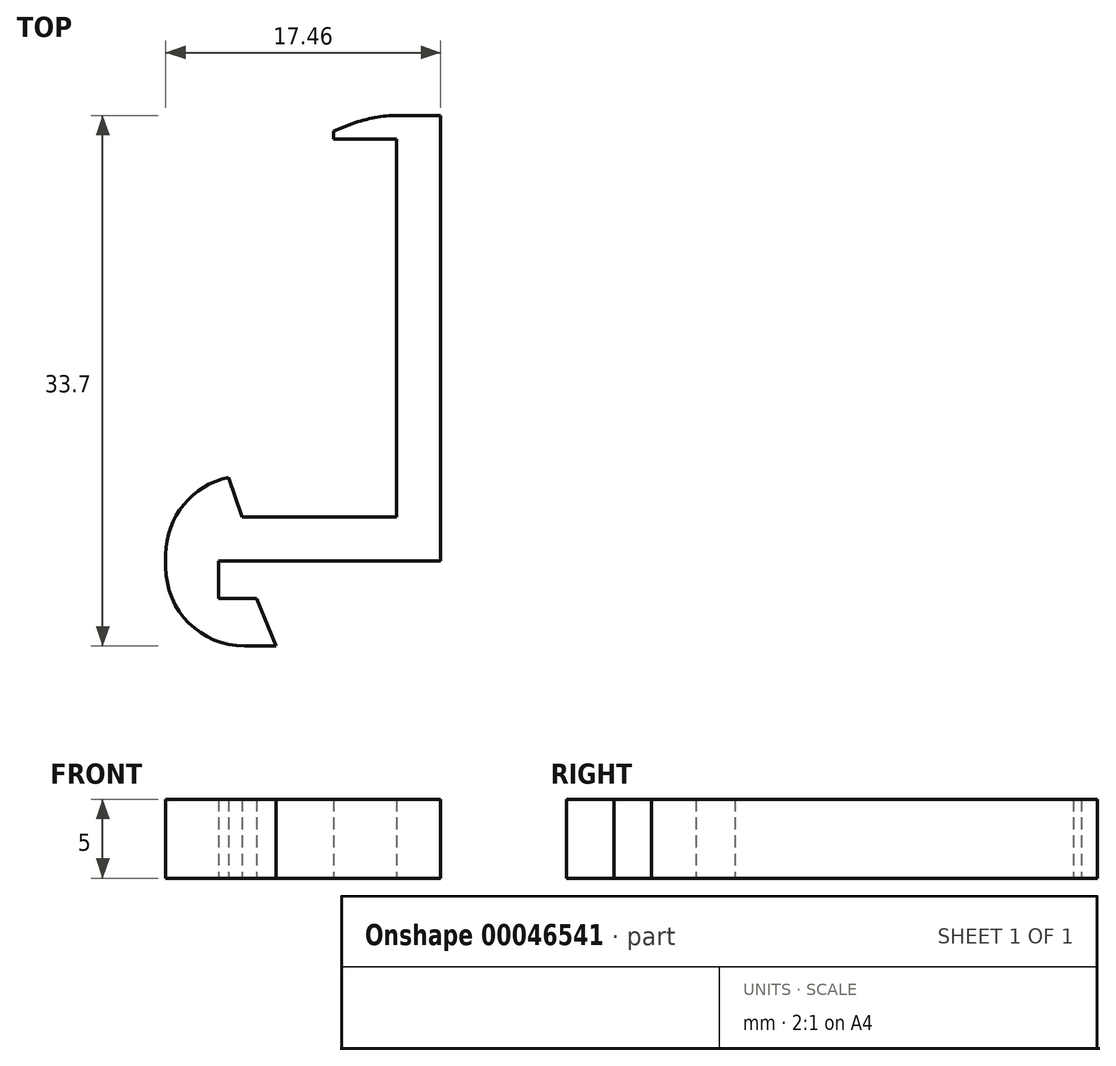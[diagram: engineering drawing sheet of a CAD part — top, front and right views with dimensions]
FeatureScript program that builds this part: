
annotation { "Feature Type Name" : "Feature", "Feature Type Description" : "" }
export const myFeature = defineFeature(function(context is Context, id is Id, definition is map)
    precondition{}
    {
        {
            var Q0;
            Q0=qCreatedBy(makeId("Top.planeOp"),FACE);
            var sketch = newSketch(context, id + "F0", { "sketchPlane" : qUnion([Q0])});
            skLineSegment(sketch, "E0", {"start": v(-10.46, -5.4) * mm, "end": v(-17.46, -5.4) * mm});
            skLineSegment(sketch, "E1", {"start": v(-17.46, -5.4) * mm, "end": v(-17.46, 5.3) * mm});
            skLineSegment(sketch, "E2", {"start": v(-17.46, 5.3) * mm, "end": v(-13.46, 5.3) * mm});
            skLineSegment(sketch, "E3", {"start": v(-13.46, 5.3) * mm, "end": v(-12.6, 2.8) * mm});
            skLineSegment(sketch, "E4", {"start": v(-12.6, 2.8) * mm, "end": v(-2.8, 2.8) * mm});
            skLineSegment(sketch, "E5", {"start": v(-2.8, 2.8) * mm, "end": v(-2.8, 26.8) * mm});
            skLineSegment(sketch, "E6", {"start": v(-2.8, 26.8) * mm, "end": v(-6.8, 26.8) * mm});
            skLineSegment(sketch, "E7", {"start": v(-14.1, 0) * mm, "end": v(-14.1, -2.4) * mm});
            skLineSegment(sketch, "E8", {"start": v(-14.1, -2.4) * mm, "end": v(-11.7, -2.4) * mm});
            skLineSegment(sketch, "E9", {"start": v(-11.7, -2.4) * mm, "end": v(-10.46, -5.4) * mm});
            skLineSegment(sketch, "E10", {"start": v(0, 28.3) * mm, "end": v(0, 0) * mm});
            skLineSegment(sketch, "E11", {"start": v(-14.1, 0) * mm, "end": v(0, 0) * mm});
            skLineSegment(sketch, "E12", {"start": v(0, 28.3) * mm, "end": v(-2.72, 28.3) * mm});
            skLineSegment(sketch, "E13", {"start": v(-6.8, 26.8) * mm, "end": v(-6.8, 27.3) * mm});
            skLineSegment(sketch, "E14", {"start": v(-6.8, 27.3) * mm, "end": v(-5.6, 27.76) * mm});
            skPoint(sketch, "E15.visualSharp", {"position": v(-4.2, 28.3) * mm});
            skArc(sketch, "E15.filletArc", {"start": v(-2.72, 28.3) * mm, "mid": v(-4.18, 28.16) * mm, "end": v(-5.6, 27.76) * mm});
            skSolve(sketch);
        }
        {
            var Q0;
            Q0=qSketchRegion(id+"F0",true);
            extrude(context, id + "F1", {"entities" : qUnion([Q0]), "depth" : 5 * mm});
        }
        {
            var Q0;
            Q0=makeQuery(id+"F1.opExtrude","SWEPT_EDGE",EDGE,{"disambiguationData":[OSD([sQuery(id+"F0.wireOp",EDGE,"E1"),sQuery(id+"F0.wireOp",EDGE,"E2")])]});
            var Q1;
            Q1=makeQuery(id+"F1.opExtrude","SWEPT_EDGE",EDGE,{"disambiguationData":[OSD([sQuery(id+"F0.wireOp",EDGE,"E0"),sQuery(id+"F0.wireOp",EDGE,"E1")])]});
            fillet(context, id + "F2", {"entities" : qUnion([Q0, Q1]), "radius" : 5 * mm, "tangentPropagation" : true, "allowEdgeOverflow" : false});
        }
    });
